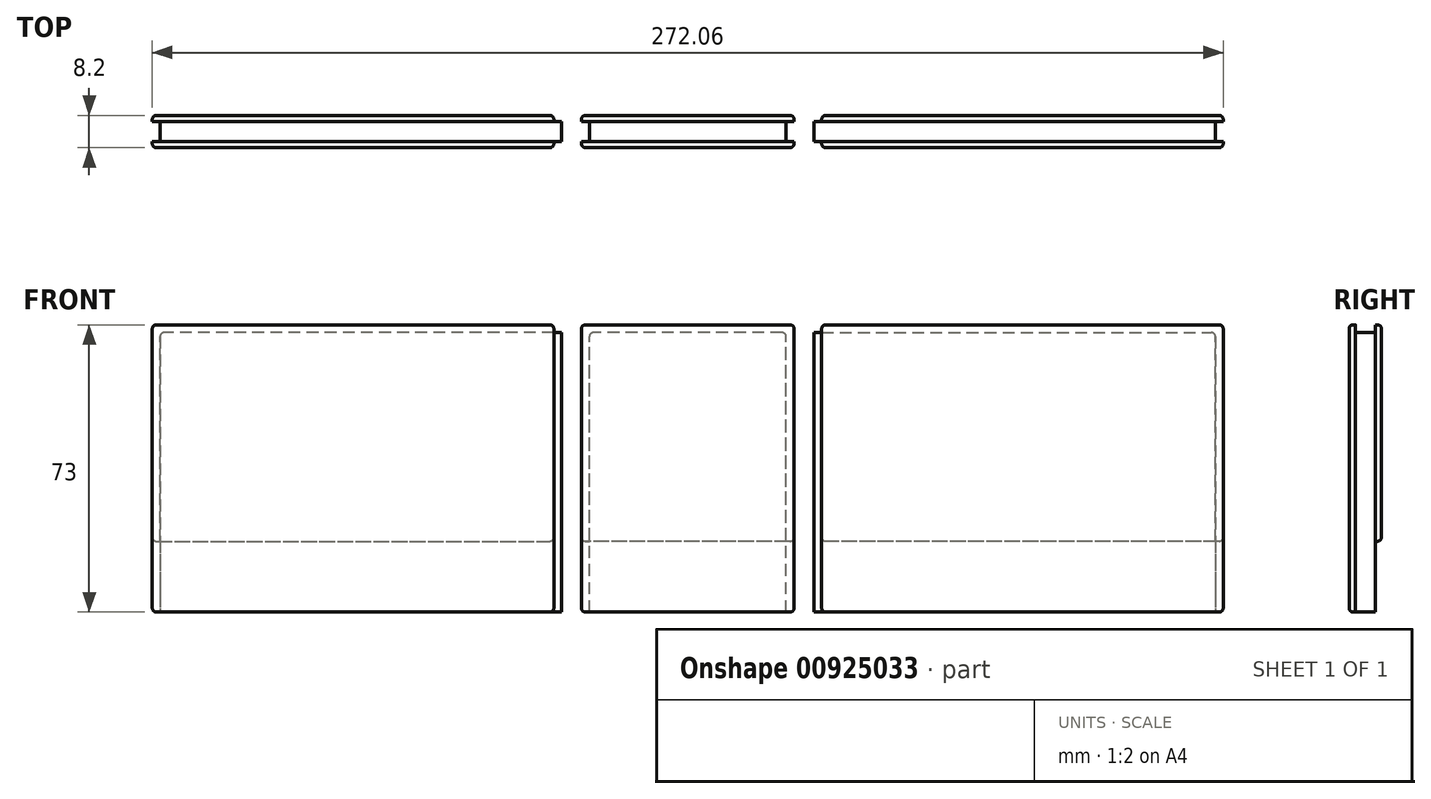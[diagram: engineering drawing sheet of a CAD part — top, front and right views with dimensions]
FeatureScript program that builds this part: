
annotation { "Feature Type Name" : "Feature", "Feature Type Description" : "" }
export const myFeature = defineFeature(function(context is Context, id is Id, definition is map)
    precondition{}
    {
        {
            var Q0;
            Q0=qCreatedBy(makeId("Front.planeOp"),FACE);
            var sketch = newSketch(context, id + "F0", { "sketchPlane" : qUnion([Q0])});
            skLineSegment(sketch, "E0.bottom", {"start": v(-25, 0) * mm, "end": v(25, 0) * mm});
            skLineSegment(sketch, "E0.top", {"start": v(-25, 18) * mm, "end": v(25, 18) * mm});
            skLineSegment(sketch, "E0.left", {"start": v(-25, 0) * mm, "end": v(-25, 18) * mm});
            skLineSegment(sketch, "E0.right", {"start": v(25, 0) * mm, "end": v(25, 18) * mm});
            skPoint(sketch, "E1", {"position": v(0, 18) * mm});
            skLineSegment(sketch, "E2.top", {"start": v(-25, 69) * mm, "end": v(25, 69) * mm});
            skLineSegment(sketch, "E2.left", {"start": v(-25, 18) * mm, "end": v(-25, 69) * mm});
            skLineSegment(sketch, "E2.right", {"start": v(25, 18) * mm, "end": v(25, 69) * mm});
            skSolve(sketch);
        }
        {
            var Q0;
            Q0=makeQuery(id+"F0.imprint","IMPRINT",FACE,{"disambiguationData":[TD([[makeQuery(id+"F0.imprint","IMPRINT",EDGE,{"derivedFrom":sQuery(id+"F0.wireOp",EDGE,"E0.top")}),1.0]])]});
            extrude(context, id + "F1", {"entities" : qUnion([Q0]), "depth" : 5 * mm, "offsetDistance" : 25 * mm});
        }
        {
            var Q0;
            Q0 = qSketchRegion(id + "F0", true);
            extrude(context, id + "F2", {"entities" : qUnion([Q0]), "operationType" : NewBodyOperationType.ADD, "depth" : 5 * mm, "offsetDistance" : 25 * mm});
        }
        {
            var Q0;
            {var subQ0=sQuery(id+"F0.wireOp",EDGE,"E2.right");var subQ1=sQuery(id+"F0.wireOp",EDGE,"E2.left");var subQ2=sQuery(id+"F0.wireOp",EDGE,"E2.top");Q0=makeQuery(id+"F2.boolean.opBoolean","MERGE",FACE,{"derivedFrom":[makeQuery(id+"F1.opExtrude","CAP_FACE",FACE,{"disambiguationData":[OSD([sQuery(id+"F0.wireOp",EDGE,"E0.top"),subQ2,subQ1,subQ0])],"isStart":true}),makeQuery(id+"F2.opExtrude","CAP_FACE",FACE,{"disambiguationData":[OSD([sQuery(id+"F0.wireOp",EDGE,"E0.bottom"),sQuery(id+"F0.wireOp",EDGE,"E0.left"),sQuery(id+"F0.wireOp",EDGE,"E0.right"),subQ2,subQ1,subQ0])],"isStart":true})]});}
            var sketch = newSketch(context, id + "F3", { "sketchPlane" : qUnion([Q0])});
            skLineSegment(sketch, "E3.bottom", {"start": v(-25, 69) * mm, "end": v(25, 69) * mm});
            skLineSegment(sketch, "E3.top", {"start": v(-25, 18) * mm, "end": v(25, 18) * mm});
            skLineSegment(sketch, "E3.left", {"start": v(-25, 69) * mm, "end": v(-25, 18) * mm});
            skLineSegment(sketch, "E3.right", {"start": v(25, 69) * mm, "end": v(25, 18) * mm});
            skSolve(sketch);
        }
        {
            var Q0;
            Q0=makeQuery(id+"F3.imprint","IMPRINT",FACE,{"disambiguationData":[TD([[makeQuery(id+"F3.imprint","IMPRINT",EDGE,{"derivedFrom":sQuery(id+"F3.wireOp",EDGE,"E3.bottom")}),1.0]])]});
            extrude(context, id + "F4", {"entities" : qUnion([Q0]), "operationType" : NewBodyOperationType.ADD, "depth" : 1.6 * mm, "offsetDistance" : 25 * mm});
        }
        {
            var Q0;
            {var subQ0=sQuery(id+"F0.wireOp",EDGE,"E2.right");var subQ1=sQuery(id+"F0.wireOp",EDGE,"E2.left");var subQ2=sQuery(id+"F0.wireOp",EDGE,"E2.top");Q0=makeQuery(id+"F2.boolean.opBoolean","MERGE",FACE,{"derivedFrom":[makeQuery(id+"F1.opExtrude","CAP_FACE",FACE,{"disambiguationData":[OSD([sQuery(id+"F0.wireOp",EDGE,"E0.top"),subQ2,subQ1,subQ0])],"isStart":false}),makeQuery(id+"F2.opExtrude","CAP_FACE",FACE,{"disambiguationData":[OSD([sQuery(id+"F0.wireOp",EDGE,"E0.bottom"),sQuery(id+"F0.wireOp",EDGE,"E0.left"),sQuery(id+"F0.wireOp",EDGE,"E0.right"),subQ2,subQ1,subQ0])],"isStart":false})]});}
            var sketch = newSketch(context, id + "F5", { "sketchPlane" : qUnion([Q0])});
            skLineSegment(sketch, "E4.bottom", {"start": v(-25, 69) * mm, "end": v(25, 69) * mm});
            skLineSegment(sketch, "E4.top", {"start": v(-25, 18) * mm, "end": v(25, 18) * mm});
            skLineSegment(sketch, "E4.left", {"start": v(-25, 69) * mm, "end": v(-25, 18) * mm});
            skLineSegment(sketch, "E4.right", {"start": v(25, 69) * mm, "end": v(25, 18) * mm});
            skSolve(sketch);
        }
        {
            var Q0;
            Q0=makeQuery(id+"F5.imprint","IMPRINT",FACE,{"disambiguationData":[TD([[makeQuery(id+"F5.imprint","IMPRINT",EDGE,{"derivedFrom":sQuery(id+"F5.wireOp",EDGE,"E4.bottom")}),-1.0]])]});
            extrude(context, id + "F6", {"entities" : qUnion([Q0]), "operationType" : NewBodyOperationType.ADD, "depth" : 1.6 * mm, "offsetDistance" : 25 * mm});
        }
        {
            var Q0;
            Q0=makeQuery(id+"F6.boolean.opBoolean","MERGE",FACE,{"derivedFrom":[makeQuery(id+"F4.boolean.opBoolean","MERGE",FACE,{"derivedFrom":[makeQuery(id+"F1.opExtrude","SWEPT_FACE",FACE,{"disambiguationData":[OSD([sQuery(id+"F0.wireOp",EDGE,"E2.top")])]}),makeQuery(id+"F4.opExtrude","SWEPT_FACE",FACE,{"disambiguationData":[OSD([sQuery(id+"F3.wireOp",EDGE,"E3.bottom")])]})]}),makeQuery(id+"F6.opExtrude","SWEPT_FACE",FACE,{"disambiguationData":[OSD([sQuery(id+"F5.wireOp",EDGE,"E4.bottom")])]})]});
            extrude(context, id + "F7", {"entities" : qUnion([Q0]), "operationType" : NewBodyOperationType.ADD, "depth" : 2 * mm, "offsetDistance" : 25 * mm});
        }
        {
            var Q0;
            {var subQ0=sQuery(id+"F5.wireOp",EDGE,"E4.left");var subQ1=sQuery(id+"F3.wireOp",EDGE,"E3.right");var subQ2=sQuery(id+"F0.wireOp",EDGE,"E2.left");Q0=makeQuery(id+"F7.boolean.opBoolean","MERGE",FACE,{"derivedFrom":[makeQuery(id+"F6.boolean.opBoolean","MERGE",FACE,{"derivedFrom":[makeQuery(id+"F4.boolean.opBoolean","MERGE",FACE,{"derivedFrom":[makeQuery(id+"F2.boolean.opBoolean","MERGE",FACE,{"derivedFrom":[makeQuery(id+"F1.opExtrude","SWEPT_FACE",FACE,{"disambiguationData":[OSD([subQ2])]}),makeQuery(id+"F2.opExtrude","SWEPT_FACE",FACE,{"disambiguationData":[OSD([sQuery(id+"F0.wireOp",EDGE,"E0.left"),subQ2])]})]}),makeQuery(id+"F4.opExtrude","SWEPT_FACE",FACE,{"disambiguationData":[OSD([subQ1])]})]}),makeQuery(id+"F6.opExtrude","SWEPT_FACE",FACE,{"disambiguationData":[OSD([subQ0])]})]}),makeQuery(id+"F7.opExtrude","SWEPT_FACE",FACE,{"disambiguationData":[OSD([sQuery(id+"F0.wireOp",EDGE,"E2.top"),subQ2,sQuery(id+"F3.wireOp",EDGE,"E3.bottom"),subQ1,sQuery(id+"F5.wireOp",EDGE,"E4.bottom"),subQ0])]})]});}
            var sketch = newSketch(context, id + "F8", { "sketchPlane" : qUnion([Q0])});
            skLineSegment(sketch, "E5", {"start": v(0, 18) * mm, "end": v(0, 71) * mm});
            skLineSegment(sketch, "E6", {"start": v(5, 18) * mm, "end": v(5, 71) * mm});
            skSolve(sketch);
        }
        {
            var Q0;
            Q0 = qSketchRegion(id + "F8", true);
            var Q1;
            {var subQ0=sQuery(id+"F8.wireOp",EDGE,"E5");Q1=makeQuery(id+"F8.imprint","IMPRINT",FACE,{"disambiguationData":[TD([[makeQuery(id+"F8.imprint","IMPRINT",EDGE,{"derivedFrom":subQ0}),1.0]])]});}
            var Q2;
            {var subQ0=sQuery(id+"F8.wireOp",EDGE,"E6");Q2=makeQuery(id+"F8.imprint","IMPRINT",FACE,{"disambiguationData":[TD([[makeQuery(id+"F8.imprint","IMPRINT",EDGE,{"derivedFrom":subQ0}),-1.0]])]});}
            extrude(context, id + "F9", {"entities" : qUnion([Q0, Q1, Q2]), "operationType" : NewBodyOperationType.ADD, "depth" : 2 * mm, "offsetDistance" : 25 * mm});
        }
        {
            var Q0;
            {var subQ0=sQuery(id+"F5.wireOp",EDGE,"E4.right");var subQ1=sQuery(id+"F3.wireOp",EDGE,"E3.left");var subQ2=sQuery(id+"F0.wireOp",EDGE,"E2.right");Q0=makeQuery(id+"F7.boolean.opBoolean","MERGE",FACE,{"derivedFrom":[makeQuery(id+"F6.boolean.opBoolean","MERGE",FACE,{"derivedFrom":[makeQuery(id+"F4.boolean.opBoolean","MERGE",FACE,{"derivedFrom":[makeQuery(id+"F2.boolean.opBoolean","MERGE",FACE,{"derivedFrom":[makeQuery(id+"F1.opExtrude","SWEPT_FACE",FACE,{"disambiguationData":[OSD([subQ2])]}),makeQuery(id+"F2.opExtrude","SWEPT_FACE",FACE,{"disambiguationData":[OSD([sQuery(id+"F0.wireOp",EDGE,"E0.right"),subQ2])]})]}),makeQuery(id+"F4.opExtrude","SWEPT_FACE",FACE,{"disambiguationData":[OSD([subQ1])]})]}),makeQuery(id+"F6.opExtrude","SWEPT_FACE",FACE,{"disambiguationData":[OSD([subQ0])]})]}),makeQuery(id+"F7.opExtrude","SWEPT_FACE",FACE,{"disambiguationData":[OSD([sQuery(id+"F0.wireOp",EDGE,"E2.top"),subQ2,sQuery(id+"F3.wireOp",EDGE,"E3.bottom"),subQ1,sQuery(id+"F5.wireOp",EDGE,"E4.bottom"),subQ0])]})]});}
            var sketch = newSketch(context, id + "F10", { "sketchPlane" : qUnion([Q0])});
            skLineSegment(sketch, "E7", {"start": v(-5, 18) * mm, "end": v(-5, 71) * mm});
            skLineSegment(sketch, "E8", {"start": v(0, 18) * mm, "end": v(0, 71) * mm});
            skSolve(sketch);
        }
        {
            var Q0;
            {var subQ0=sQuery(id+"F10.wireOp",EDGE,"E7");Q0=makeQuery(id+"F10.imprint","IMPRINT",FACE,{"disambiguationData":[TD([[makeQuery(id+"F10.imprint","IMPRINT",EDGE,{"derivedFrom":subQ0}),1.0]])]});}
            var Q1;
            {var subQ0=sQuery(id+"F10.wireOp",EDGE,"E8");Q1=makeQuery(id+"F10.imprint","IMPRINT",FACE,{"disambiguationData":[TD([[makeQuery(id+"F10.imprint","IMPRINT",EDGE,{"derivedFrom":subQ0}),-1.0]])]});}
            extrude(context, id + "F11", {"entities" : qUnion([Q0, Q1]), "operationType" : NewBodyOperationType.ADD, "depth" : 2 * mm, "offsetDistance" : 25 * mm});
        }
        {
            var Q0;
            {var subQ0=sQuery(id+"F0.wireOp",EDGE,"E2.right");var subQ1=sQuery(id+"F0.wireOp",EDGE,"E2.left");var subQ2=sQuery(id+"F0.wireOp",EDGE,"E2.top");Q0=makeQuery(id+"F2.boolean.opBoolean","MERGE",FACE,{"derivedFrom":[makeQuery(id+"F1.opExtrude","CAP_FACE",FACE,{"disambiguationData":[OSD([sQuery(id+"F0.wireOp",EDGE,"E0.top"),subQ2,subQ1,subQ0])],"isStart":false}),makeQuery(id+"F2.opExtrude","CAP_FACE",FACE,{"disambiguationData":[OSD([sQuery(id+"F0.wireOp",EDGE,"E0.bottom"),sQuery(id+"F0.wireOp",EDGE,"E0.left"),sQuery(id+"F0.wireOp",EDGE,"E0.right"),subQ2,subQ1,subQ0])],"isStart":false})]});}
            extrude(context, id + "F12", {"entities" : qUnion([Q0]), "operationType" : NewBodyOperationType.ADD, "depth" : 1.6 * mm, "offsetDistance" : 25 * mm});
        }
        {
            var Q0;
            {var subQ1=sQuery(id+"F5.wireOp",EDGE,"E4.right");var subQ5=sQuery(id+"F0.wireOp",EDGE,"E2.right");var subQ7=sQuery(id+"F0.wireOp",EDGE,"E2.left");var subQ8=sQuery(id+"F0.wireOp",EDGE,"E0.right");var subQ9=sQuery(id+"F0.wireOp",EDGE,"E0.left");var subQ10=sQuery(id+"F5.wireOp",EDGE,"E4.left");var subQ11=sQuery(id+"F5.wireOp",EDGE,"E4.top");Q0=makeQuery(id+"F12.boolean.opBoolean","SPLIT",FACE,{"disambiguationData":[TD([makeQuery(id+"F1.opExtrude","SWEPT_FACE",FACE,{"disambiguationData":[OSD([subQ5])]})])],"derivedFrom":makeQuery(id+"F11.boolean.opBoolean","MERGE",FACE,{"derivedFrom":[makeQuery(id+"F9.boolean.opBoolean","MERGE",FACE,{"derivedFrom":[makeQuery(id+"F6.opExtrude","SWEPT_FACE",FACE,{"disambiguationData":[OSD([subQ11])]}),makeQuery(id+"F9.opExtrude","SWEPT_FACE",FACE,{"disambiguationData":[OSD([subQ9,subQ7,subQ11,subQ10])]})]}),makeQuery(id+"F11.opExtrude","SWEPT_FACE",FACE,{"disambiguationData":[OSD([subQ8,subQ5,subQ11,subQ1])]})]})});}
            var Q1;
            {var subQ1=sQuery(id+"F5.wireOp",EDGE,"E4.left");var subQ2=sQuery(id+"F5.wireOp",EDGE,"E4.top");var subQ6=sQuery(id+"F0.wireOp",EDGE,"E2.left");var subQ8=sQuery(id+"F0.wireOp",EDGE,"E0.left");var subQ9=sQuery(id+"F5.wireOp",EDGE,"E4.right");var subQ10=sQuery(id+"F0.wireOp",EDGE,"E2.right");var subQ11=sQuery(id+"F0.wireOp",EDGE,"E0.right");Q1=makeQuery(id+"F12.boolean.opBoolean","SPLIT",FACE,{"disambiguationData":[TD([makeQuery(id+"F1.opExtrude","SWEPT_FACE",FACE,{"disambiguationData":[OSD([subQ6])]})])],"derivedFrom":makeQuery(id+"F11.boolean.opBoolean","MERGE",FACE,{"derivedFrom":[makeQuery(id+"F9.boolean.opBoolean","MERGE",FACE,{"derivedFrom":[makeQuery(id+"F6.opExtrude","SWEPT_FACE",FACE,{"disambiguationData":[OSD([subQ2])]}),makeQuery(id+"F9.opExtrude","SWEPT_FACE",FACE,{"disambiguationData":[OSD([subQ8,subQ6,subQ2,subQ1])]})]}),makeQuery(id+"F11.opExtrude","SWEPT_FACE",FACE,{"disambiguationData":[OSD([subQ11,subQ10,subQ2,subQ9])]})]})});}
            var Q2;
            {var subQ0=sQuery(id+"F0.wireOp",EDGE,"E0.bottom");Q2=makeQuery(id+"F12.boolean.opBoolean","MERGE",FACE,{"derivedFrom":[makeQuery(id+"F2.opExtrude","SWEPT_FACE",FACE,{"disambiguationData":[OSD([subQ0])]}),makeQuery(id+"F12.opExtrude","SWEPT_FACE",FACE,{"disambiguationData":[OSD([subQ0])]})]});}
            extrude(context, id + "F13", {"entities" : qUnion([Q0, Q1]), "operationType" : NewBodyOperationType.ADD, "endBound" : BoundingType.UP_TO_SURFACE, "depth" : 25 * mm, "endBoundEntityFace" : qUnion([Q2]), "offsetDistance" : 25 * mm});
        }
        {
            var Q0;
            {var subQ0=sQuery(id+"F5.wireOp",EDGE,"E4.right");var subQ1=sQuery(id+"F5.wireOp",EDGE,"E4.bottom");var subQ2=sQuery(id+"F3.wireOp",EDGE,"E3.left");var subQ3=sQuery(id+"F3.wireOp",EDGE,"E3.bottom");var subQ4=sQuery(id+"F0.wireOp",EDGE,"E2.right");var subQ5=sQuery(id+"F0.wireOp",EDGE,"E2.top");var subQ6=makeQuery(id+"F7.opExtrude","CAP_EDGE",EDGE,{"disambiguationData":[OSD([subQ5,subQ4,subQ3,subQ2,subQ1,subQ0])],"isStart":false});var subQ7=sQuery(id+"F5.wireOp",EDGE,"E4.left");var subQ8=sQuery(id+"F3.wireOp",EDGE,"E3.right");var subQ9=sQuery(id+"F0.wireOp",EDGE,"E2.left");var subQ10=makeQuery(id+"F7.opExtrude","CAP_EDGE",EDGE,{"disambiguationData":[OSD([subQ5,subQ9,subQ3,subQ8,subQ1,subQ7])],"isStart":false});Q0=makeQuery(id+"F11.boolean.opBoolean","MERGE",FACE,{"derivedFrom":[makeQuery(id+"F9.boolean.opBoolean","MERGE",FACE,{"derivedFrom":[makeQuery(id+"F7.opExtrude","CAP_FACE",FACE,{"disambiguationData":[OSD([subQ5,subQ3,subQ1])],"isStart":false}),makeQuery(id+"F9.opExtrude","SWEPT_FACE",FACE,{"disambiguationData":[OSD([subQ5,subQ9,subQ3,subQ8,subQ1,subQ7]),TDD([makeQuery(id+"F8.imprint","IMPRINT",EDGE,{"disambiguationData":[TD([[makeQuery(id+"F8.imprint","INTERSECT",VERTEX,{"derivedFrom":[subQ10,sQuery(id+"F8.wireOp",EDGE,"E5")]}),-1.0]])],"derivedFrom":subQ10})])]}),makeQuery(id+"F9.opExtrude","SWEPT_FACE",FACE,{"disambiguationData":[OSD([subQ5,subQ9,subQ3,subQ8,subQ1,subQ7]),TDD([makeQuery(id+"F8.imprint","IMPRINT",EDGE,{"disambiguationData":[TD([[makeQuery(id+"F8.imprint","INTERSECT",VERTEX,{"derivedFrom":[subQ10,sQuery(id+"F8.wireOp",EDGE,"E6")]}),1.0]])],"derivedFrom":subQ10})])]})]}),makeQuery(id+"F11.opExtrude","SWEPT_FACE",FACE,{"disambiguationData":[OSD([subQ5,subQ4,subQ3,subQ2,subQ1,subQ0]),TDD([makeQuery(id+"F10.imprint","IMPRINT",EDGE,{"disambiguationData":[TD([[makeQuery(id+"F10.imprint","INTERSECT",VERTEX,{"derivedFrom":[subQ6,sQuery(id+"F10.wireOp",EDGE,"E8")]}),-1.0]])],"derivedFrom":subQ6})])]}),makeQuery(id+"F11.opExtrude","SWEPT_FACE",FACE,{"disambiguationData":[OSD([subQ5,subQ4,subQ3,subQ2,subQ1,subQ0]),TDD([makeQuery(id+"F10.imprint","IMPRINT",EDGE,{"disambiguationData":[TD([[makeQuery(id+"F10.imprint","INTERSECT",VERTEX,{"derivedFrom":[subQ6,sQuery(id+"F10.wireOp",EDGE,"E7")]}),1.0]])],"derivedFrom":subQ6})])]})]});}
            var sketch = newSketch(context, id + "F14", { "sketchPlane" : qUnion([Q0])});
            skLineSegment(sketch, "E9", {"start": v(-25, 0) * mm, "end": v(25, 0) * mm});
            skLineSegment(sketch, "E10", {"start": v(25, -5) * mm, "end": v(-25, -5) * mm});
            skSolve(sketch);
        }
        {
            var Q0;
            Q0=makeQuery(id+"F14.imprint","IMPRINT",FACE,{"disambiguationData":[TD([[makeQuery(id+"F14.imprint","IMPRINT",EDGE,{"derivedFrom":sQuery(id+"F14.wireOp",EDGE,"E10")}),1.0]])]});
            var Q1;
            Q1=makeQuery(id+"F14.imprint","IMPRINT",FACE,{"disambiguationData":[TD([[makeQuery(id+"F14.imprint","IMPRINT",EDGE,{"derivedFrom":sQuery(id+"F14.wireOp",EDGE,"E9")}),1.0]])]});
            extrude(context, id + "F15", {"entities" : qUnion([Q0, Q1]), "operationType" : NewBodyOperationType.ADD, "depth" : 2 * mm, "offsetDistance" : 25 * mm});
        }
        {
            var Q0;
            Q0=makeQuery(id+"F11.opExtrude","CAP_EDGE",EDGE,{"disambiguationData":[OSD([sQuery(id+"F3.wireOp",EDGE,"E3.bottom"),sQuery(id+"F3.wireOp",EDGE,"E3.left")])],"isStart":false});
            var Q1;
            Q1=makeQuery(id+"F11.opExtrude","CAP_EDGE",EDGE,{"disambiguationData":[OSD([sQuery(id+"F5.wireOp",EDGE,"E4.bottom"),sQuery(id+"F5.wireOp",EDGE,"E4.right")])],"isStart":false});
            var Q2;
            Q2=makeQuery(id+"F9.opExtrude","CAP_EDGE",EDGE,{"disambiguationData":[OSD([sQuery(id+"F5.wireOp",EDGE,"E4.bottom"),sQuery(id+"F5.wireOp",EDGE,"E4.left")])],"isStart":false});
            var Q3;
            Q3=makeQuery(id+"F9.opExtrude","CAP_EDGE",EDGE,{"disambiguationData":[OSD([sQuery(id+"F3.wireOp",EDGE,"E3.bottom"),sQuery(id+"F3.wireOp",EDGE,"E3.right")])],"isStart":false});
            var Q4;
            {var subQ0=sQuery(id+"F3.wireOp",EDGE,"E3.top");var subQ1=sQuery(id+"F3.wireOp",EDGE,"E3.bottom");Q4=makeQuery(id+"F11.boolean.opBoolean","MERGE",EDGE,{"derivedFrom":[makeQuery(id+"F9.boolean.opBoolean","MERGE",EDGE,{"derivedFrom":[makeQuery(id+"F4.opExtrude","CAP_EDGE",EDGE,{"disambiguationData":[OSD([subQ0])],"isStart":false}),makeQuery(id+"F9.opExtrude","SWEPT_EDGE",EDGE,{"disambiguationData":[OSD([sQuery(id+"F0.wireOp",EDGE,"E0.left"),sQuery(id+"F0.wireOp",EDGE,"E2.left"),subQ1,subQ0,sQuery(id+"F3.wireOp",EDGE,"E3.right")])]})]}),makeQuery(id+"F11.opExtrude","SWEPT_EDGE",EDGE,{"disambiguationData":[OSD([sQuery(id+"F0.wireOp",EDGE,"E0.right"),sQuery(id+"F0.wireOp",EDGE,"E2.right"),subQ1,subQ0,sQuery(id+"F3.wireOp",EDGE,"E3.left")])]})]});}
            var Q5;
            {var subQ0=sQuery(id+"F5.wireOp",EDGE,"E4.top");var subQ1=sQuery(id+"F5.wireOp",EDGE,"E4.bottom");Q5=makeQuery(id+"F11.boolean.opBoolean","MERGE",EDGE,{"derivedFrom":[makeQuery(id+"F9.boolean.opBoolean","MERGE",EDGE,{"derivedFrom":[makeQuery(id+"F6.opExtrude","CAP_EDGE",EDGE,{"disambiguationData":[OSD([subQ0])],"isStart":false}),makeQuery(id+"F9.opExtrude","SWEPT_EDGE",EDGE,{"disambiguationData":[OSD([sQuery(id+"F0.wireOp",EDGE,"E0.left"),sQuery(id+"F0.wireOp",EDGE,"E2.left"),subQ1,subQ0,sQuery(id+"F5.wireOp",EDGE,"E4.left")])]})]}),makeQuery(id+"F11.opExtrude","SWEPT_EDGE",EDGE,{"disambiguationData":[OSD([sQuery(id+"F0.wireOp",EDGE,"E0.right"),sQuery(id+"F0.wireOp",EDGE,"E2.right"),subQ1,subQ0,sQuery(id+"F5.wireOp",EDGE,"E4.right")])]})]});}
            var Q6;
            Q6=makeQuery(id+"F7.opExtrude","CAP_EDGE",EDGE,{"disambiguationData":[OSD([sQuery(id+"F0.wireOp",EDGE,"E2.top"),sQuery(id+"F0.wireOp",EDGE,"E2.left"),sQuery(id+"F3.wireOp",EDGE,"E3.bottom"),sQuery(id+"F3.wireOp",EDGE,"E3.right"),sQuery(id+"F5.wireOp",EDGE,"E4.bottom"),sQuery(id+"F5.wireOp",EDGE,"E4.left")])],"isStart":false});
            var Q7;
            Q7=makeQuery(id+"F7.opExtrude","CAP_EDGE",EDGE,{"disambiguationData":[OSD([sQuery(id+"F0.wireOp",EDGE,"E2.top"),sQuery(id+"F0.wireOp",EDGE,"E2.right"),sQuery(id+"F3.wireOp",EDGE,"E3.bottom"),sQuery(id+"F3.wireOp",EDGE,"E3.left"),sQuery(id+"F5.wireOp",EDGE,"E4.bottom"),sQuery(id+"F5.wireOp",EDGE,"E4.right")])],"isStart":false});
            var Q8;
            {var subQ0=sQuery(id+"F3.wireOp",EDGE,"E3.left");var subQ1=sQuery(id+"F3.wireOp",EDGE,"E3.bottom");var subQ2=sQuery(id+"F5.wireOp",EDGE,"E4.right");var subQ3=sQuery(id+"F5.wireOp",EDGE,"E4.bottom");var subQ4=sQuery(id+"F0.wireOp",EDGE,"E2.right");var subQ5=sQuery(id+"F0.wireOp",EDGE,"E2.top");var subQ6=sQuery(id+"F3.wireOp",EDGE,"E3.right");var subQ7=sQuery(id+"F5.wireOp",EDGE,"E4.left");var subQ8=sQuery(id+"F0.wireOp",EDGE,"E2.left");Q8=makeQuery(id+"F11.boolean.opBoolean","MERGE",EDGE,{"derivedFrom":[makeQuery(id+"F9.boolean.opBoolean","MERGE",EDGE,{"derivedFrom":[makeQuery(id+"F7.opExtrude","CAP_EDGE",EDGE,{"disambiguationData":[OSD([subQ1])],"isStart":false}),makeQuery(id+"F9.opExtrude","SWEPT_EDGE",EDGE,{"disambiguationData":[OSD([subQ5,subQ8,subQ1,subQ6,subQ3,subQ7]),TDD([makeQuery(id+"F8.imprint","INTERSECT",VERTEX,{"derivedFrom":[makeQuery(id+"F7.opExtrude","CAP_EDGE",EDGE,{"disambiguationData":[OSD([subQ5,subQ8,subQ1,subQ6,subQ3,subQ7])],"isStart":false}),makeQuery(id+"F7.boolean.opBoolean","MERGE",EDGE,{"derivedFrom":[makeQuery(id+"F4.opExtrude","CAP_EDGE",EDGE,{"disambiguationData":[OSD([subQ6])],"isStart":false}),makeQuery(id+"F7.opExtrude","SWEPT_EDGE",EDGE,{"disambiguationData":[OSD([subQ1,subQ6])]})]})]})])]})]}),makeQuery(id+"F11.opExtrude","SWEPT_EDGE",EDGE,{"disambiguationData":[OSD([subQ5,subQ4,subQ1,subQ0,subQ3,subQ2]),TDD([makeQuery(id+"F10.imprint","INTERSECT",VERTEX,{"derivedFrom":[makeQuery(id+"F7.opExtrude","CAP_EDGE",EDGE,{"disambiguationData":[OSD([subQ5,subQ4,subQ1,subQ0,subQ3,subQ2])],"isStart":false}),makeQuery(id+"F7.boolean.opBoolean","MERGE",EDGE,{"derivedFrom":[makeQuery(id+"F4.opExtrude","CAP_EDGE",EDGE,{"disambiguationData":[OSD([subQ0])],"isStart":false}),makeQuery(id+"F7.opExtrude","SWEPT_EDGE",EDGE,{"disambiguationData":[OSD([subQ1,subQ0])]})]})]})])]})]});}
            var Q9;
            {var subQ0=sQuery(id+"F5.wireOp",EDGE,"E4.right");var subQ1=sQuery(id+"F5.wireOp",EDGE,"E4.bottom");var subQ2=sQuery(id+"F3.wireOp",EDGE,"E3.left");var subQ3=sQuery(id+"F3.wireOp",EDGE,"E3.bottom");var subQ4=sQuery(id+"F0.wireOp",EDGE,"E2.right");var subQ5=sQuery(id+"F0.wireOp",EDGE,"E2.top");var subQ6=sQuery(id+"F5.wireOp",EDGE,"E4.left");var subQ7=sQuery(id+"F3.wireOp",EDGE,"E3.right");var subQ8=sQuery(id+"F0.wireOp",EDGE,"E2.left");Q9=makeQuery(id+"F11.boolean.opBoolean","MERGE",EDGE,{"derivedFrom":[makeQuery(id+"F9.boolean.opBoolean","MERGE",EDGE,{"derivedFrom":[makeQuery(id+"F7.opExtrude","CAP_EDGE",EDGE,{"disambiguationData":[OSD([subQ1])],"isStart":false}),makeQuery(id+"F9.opExtrude","SWEPT_EDGE",EDGE,{"disambiguationData":[OSD([subQ5,subQ8,subQ3,subQ7,subQ1,subQ6]),TDD([makeQuery(id+"F8.imprint","INTERSECT",VERTEX,{"derivedFrom":[makeQuery(id+"F7.opExtrude","CAP_EDGE",EDGE,{"disambiguationData":[OSD([subQ5,subQ8,subQ3,subQ7,subQ1,subQ6])],"isStart":false}),makeQuery(id+"F7.boolean.opBoolean","MERGE",EDGE,{"derivedFrom":[makeQuery(id+"F6.opExtrude","CAP_EDGE",EDGE,{"disambiguationData":[OSD([subQ6])],"isStart":false}),makeQuery(id+"F7.opExtrude","SWEPT_EDGE",EDGE,{"disambiguationData":[OSD([subQ1,subQ6])]})]})]})])]})]}),makeQuery(id+"F11.opExtrude","SWEPT_EDGE",EDGE,{"disambiguationData":[OSD([subQ5,subQ4,subQ3,subQ2,subQ1,subQ0]),TDD([makeQuery(id+"F10.imprint","INTERSECT",VERTEX,{"derivedFrom":[makeQuery(id+"F7.opExtrude","CAP_EDGE",EDGE,{"disambiguationData":[OSD([subQ5,subQ4,subQ3,subQ2,subQ1,subQ0])],"isStart":false}),makeQuery(id+"F7.boolean.opBoolean","MERGE",EDGE,{"derivedFrom":[makeQuery(id+"F6.opExtrude","CAP_EDGE",EDGE,{"disambiguationData":[OSD([subQ0])],"isStart":false}),makeQuery(id+"F7.opExtrude","SWEPT_EDGE",EDGE,{"disambiguationData":[OSD([subQ1,subQ0])]})]})]})])]})]});}
            var Q10;
            {var subQ0=sQuery(id+"F3.wireOp",EDGE,"E3.right");var subQ1=sQuery(id+"F3.wireOp",EDGE,"E3.bottom");var subQ2=sQuery(id+"F5.wireOp",EDGE,"E4.left");var subQ3=sQuery(id+"F5.wireOp",EDGE,"E4.bottom");var subQ4=sQuery(id+"F0.wireOp",EDGE,"E2.left");var subQ5=sQuery(id+"F0.wireOp",EDGE,"E2.top");var subQ6=makeQuery(id+"F7.opExtrude","CAP_EDGE",EDGE,{"disambiguationData":[OSD([subQ5,subQ4,subQ1,subQ0,subQ3,subQ2])],"isStart":false});Q10=makeQuery(id+"F9.opExtrude","CAP_EDGE",EDGE,{"disambiguationData":[OSD([subQ5,subQ4,subQ1,subQ0,subQ3,subQ2]),TDD([makeQuery(id+"F8.imprint","IMPRINT",EDGE,{"disambiguationData":[TD([[makeQuery(id+"F8.imprint","INTERSECT",VERTEX,{"derivedFrom":[subQ6,sQuery(id+"F8.wireOp",EDGE,"E5")]}),-1.0]])],"derivedFrom":subQ6})])],"isStart":false});}
            var Q11;
            {var subQ0=sQuery(id+"F5.wireOp",EDGE,"E4.left");var subQ1=sQuery(id+"F5.wireOp",EDGE,"E4.bottom");var subQ2=sQuery(id+"F3.wireOp",EDGE,"E3.right");var subQ3=sQuery(id+"F3.wireOp",EDGE,"E3.bottom");var subQ4=sQuery(id+"F0.wireOp",EDGE,"E2.left");var subQ5=sQuery(id+"F0.wireOp",EDGE,"E2.top");var subQ6=makeQuery(id+"F7.opExtrude","CAP_EDGE",EDGE,{"disambiguationData":[OSD([subQ5,subQ4,subQ3,subQ2,subQ1,subQ0])],"isStart":false});Q11=makeQuery(id+"F9.opExtrude","CAP_EDGE",EDGE,{"disambiguationData":[OSD([subQ5,subQ4,subQ3,subQ2,subQ1,subQ0]),TDD([makeQuery(id+"F8.imprint","IMPRINT",EDGE,{"disambiguationData":[TD([[makeQuery(id+"F8.imprint","INTERSECT",VERTEX,{"derivedFrom":[subQ6,sQuery(id+"F8.wireOp",EDGE,"E6")]}),1.0]])],"derivedFrom":subQ6})])],"isStart":false});}
            var Q12;
            {var subQ0=sQuery(id+"F3.wireOp",EDGE,"E3.left");var subQ1=sQuery(id+"F3.wireOp",EDGE,"E3.bottom");var subQ2=sQuery(id+"F5.wireOp",EDGE,"E4.right");var subQ3=sQuery(id+"F5.wireOp",EDGE,"E4.bottom");var subQ4=sQuery(id+"F0.wireOp",EDGE,"E2.right");var subQ5=sQuery(id+"F0.wireOp",EDGE,"E2.top");var subQ6=makeQuery(id+"F7.opExtrude","CAP_EDGE",EDGE,{"disambiguationData":[OSD([subQ5,subQ4,subQ1,subQ0,subQ3,subQ2])],"isStart":false});Q12=makeQuery(id+"F11.opExtrude","CAP_EDGE",EDGE,{"disambiguationData":[OSD([subQ5,subQ4,subQ1,subQ0,subQ3,subQ2]),TDD([makeQuery(id+"F10.imprint","IMPRINT",EDGE,{"disambiguationData":[TD([[makeQuery(id+"F10.imprint","INTERSECT",VERTEX,{"derivedFrom":[subQ6,sQuery(id+"F10.wireOp",EDGE,"E8")]}),-1.0]])],"derivedFrom":subQ6})])],"isStart":false});}
            var Q13;
            {var subQ0=sQuery(id+"F5.wireOp",EDGE,"E4.right");var subQ1=sQuery(id+"F5.wireOp",EDGE,"E4.bottom");var subQ2=sQuery(id+"F3.wireOp",EDGE,"E3.left");var subQ3=sQuery(id+"F3.wireOp",EDGE,"E3.bottom");var subQ4=sQuery(id+"F0.wireOp",EDGE,"E2.right");var subQ5=sQuery(id+"F0.wireOp",EDGE,"E2.top");var subQ6=makeQuery(id+"F7.opExtrude","CAP_EDGE",EDGE,{"disambiguationData":[OSD([subQ5,subQ4,subQ3,subQ2,subQ1,subQ0])],"isStart":false});Q13=makeQuery(id+"F11.opExtrude","CAP_EDGE",EDGE,{"disambiguationData":[OSD([subQ5,subQ4,subQ3,subQ2,subQ1,subQ0]),TDD([makeQuery(id+"F10.imprint","IMPRINT",EDGE,{"disambiguationData":[TD([[makeQuery(id+"F10.imprint","INTERSECT",VERTEX,{"derivedFrom":[subQ6,sQuery(id+"F10.wireOp",EDGE,"E7")]}),1.0]])],"derivedFrom":subQ6})])],"isStart":false});}
            var Q14;
            {var subQ0=sQuery(id+"F5.wireOp",EDGE,"E4.left");var subQ1=sQuery(id+"F5.wireOp",EDGE,"E4.bottom");var subQ3=sQuery(id+"F5.wireOp",EDGE,"E4.right");var subQ6=sQuery(id+"F0.wireOp",EDGE,"E2.right");var subQ8=sQuery(id+"F0.wireOp",EDGE,"E2.left");var subQ9=sQuery(id+"F0.wireOp",EDGE,"E0.right");var subQ10=sQuery(id+"F0.wireOp",EDGE,"E0.left");var subQ11=sQuery(id+"F0.wireOp",EDGE,"E0.bottom");var subQ13=sQuery(id+"F5.wireOp",EDGE,"E4.top");var subQ20=makeQuery(id+"F11.boolean.opBoolean","MERGE",EDGE,{"derivedFrom":[makeQuery(id+"F9.boolean.opBoolean","MERGE",EDGE,{"derivedFrom":[makeQuery(id+"F6.opExtrude","CAP_EDGE",EDGE,{"disambiguationData":[OSD([subQ13])],"isStart":false}),makeQuery(id+"F9.opExtrude","SWEPT_EDGE",EDGE,{"disambiguationData":[OSD([subQ10,subQ8,subQ1,subQ13,subQ0])]})]}),makeQuery(id+"F11.opExtrude","SWEPT_EDGE",EDGE,{"disambiguationData":[OSD([subQ9,subQ6,subQ1,subQ13,subQ3])]})]});Q14=makeQuery(id+"F13.boolean.opBoolean","MERGE",EDGE,{"derivedFrom":[makeQuery(id+"F12.opExtrude","CAP_EDGE",EDGE,{"disambiguationData":[OSD([subQ11])],"isStart":false}),makeQuery(id+"F13.opExtrude","CAP_EDGE",EDGE,{"disambiguationData":[OSD([subQ10,subQ9,subQ8,subQ6,subQ1,subQ13,subQ0,subQ3]),TDD([makeQuery(id+"F12.boolean.opBoolean","SPLIT",EDGE,{"disambiguationData":[TD([makeQuery(id+"F1.opExtrude","SWEPT_FACE",FACE,{"disambiguationData":[OSD([subQ8])]})])],"derivedFrom":subQ20})])],"isStart":false}),makeQuery(id+"F13.opExtrude","CAP_EDGE",EDGE,{"disambiguationData":[OSD([subQ10,subQ9,subQ8,subQ6,subQ1,subQ13,subQ0,subQ3]),TDD([makeQuery(id+"F12.boolean.opBoolean","SPLIT",EDGE,{"disambiguationData":[TD([makeQuery(id+"F1.opExtrude","SWEPT_FACE",FACE,{"disambiguationData":[OSD([subQ6])]})])],"derivedFrom":subQ20})])],"isStart":false})]});}
            var Q15;
            Q15=makeQuery(id+"F13.opExtrude","CAP_EDGE",EDGE,{"disambiguationData":[OSD([sQuery(id+"F0.wireOp",EDGE,"E0.left"),sQuery(id+"F0.wireOp",EDGE,"E2.left"),sQuery(id+"F5.wireOp",EDGE,"E4.top"),sQuery(id+"F5.wireOp",EDGE,"E4.left")])],"isStart":false});
            var Q16;
            Q16=makeQuery(id+"F13.opExtrude","CAP_EDGE",EDGE,{"disambiguationData":[OSD([sQuery(id+"F0.wireOp",EDGE,"E0.right"),sQuery(id+"F0.wireOp",EDGE,"E2.right"),sQuery(id+"F5.wireOp",EDGE,"E4.top"),sQuery(id+"F5.wireOp",EDGE,"E4.right")])],"isStart":false});
            var Q17;
            Q17=makeQuery(id+"F9.opExtrude","CAP_EDGE",EDGE,{"disambiguationData":[OSD([sQuery(id+"F0.wireOp",EDGE,"E0.left"),sQuery(id+"F0.wireOp",EDGE,"E2.left"),sQuery(id+"F3.wireOp",EDGE,"E3.top"),sQuery(id+"F3.wireOp",EDGE,"E3.right")])],"isStart":false});
            var Q18;
            Q18=makeQuery(id+"F11.opExtrude","CAP_EDGE",EDGE,{"disambiguationData":[OSD([sQuery(id+"F0.wireOp",EDGE,"E0.right"),sQuery(id+"F0.wireOp",EDGE,"E2.right"),sQuery(id+"F3.wireOp",EDGE,"E3.top"),sQuery(id+"F3.wireOp",EDGE,"E3.left")])],"isStart":false});
            var Q19;
            {var subQ0=sQuery(id+"F5.wireOp",EDGE,"E4.right");var subQ1=sQuery(id+"F5.wireOp",EDGE,"E4.bottom");var subQ2=sQuery(id+"F3.wireOp",EDGE,"E3.left");var subQ3=sQuery(id+"F3.wireOp",EDGE,"E3.bottom");var subQ4=sQuery(id+"F0.wireOp",EDGE,"E2.right");var subQ5=sQuery(id+"F0.wireOp",EDGE,"E2.top");var subQ6=sQuery(id+"F5.wireOp",EDGE,"E4.left");var subQ7=sQuery(id+"F3.wireOp",EDGE,"E3.right");var subQ8=sQuery(id+"F0.wireOp",EDGE,"E2.left");Q19=makeQuery(id+"F15.opExtrude","CAP_EDGE",EDGE,{"disambiguationData":[OSD([subQ5,subQ8,subQ4,subQ3,subQ2,subQ7,subQ1,subQ6,subQ0]),TDD([makeQuery(id+"F14.imprint","IMPRINT",EDGE,{"derivedFrom":makeQuery(id+"F11.boolean.opBoolean","MERGE",EDGE,{"derivedFrom":[makeQuery(id+"F9.boolean.opBoolean","MERGE",EDGE,{"derivedFrom":[makeQuery(id+"F7.opExtrude","CAP_EDGE",EDGE,{"disambiguationData":[OSD([subQ1])],"isStart":false}),makeQuery(id+"F9.opExtrude","SWEPT_EDGE",EDGE,{"disambiguationData":[OSD([subQ5,subQ8,subQ3,subQ7,subQ1,subQ6]),TDD([makeQuery(id+"F8.imprint","INTERSECT",VERTEX,{"derivedFrom":[makeQuery(id+"F7.opExtrude","CAP_EDGE",EDGE,{"disambiguationData":[OSD([subQ5,subQ8,subQ3,subQ7,subQ1,subQ6])],"isStart":false}),makeQuery(id+"F7.boolean.opBoolean","MERGE",EDGE,{"derivedFrom":[makeQuery(id+"F6.opExtrude","CAP_EDGE",EDGE,{"disambiguationData":[OSD([subQ6])],"isStart":false}),makeQuery(id+"F7.opExtrude","SWEPT_EDGE",EDGE,{"disambiguationData":[OSD([subQ1,subQ6])]})]})]})])]})]}),makeQuery(id+"F11.opExtrude","SWEPT_EDGE",EDGE,{"disambiguationData":[OSD([subQ5,subQ4,subQ3,subQ2,subQ1,subQ0]),TDD([makeQuery(id+"F10.imprint","INTERSECT",VERTEX,{"derivedFrom":[makeQuery(id+"F7.opExtrude","CAP_EDGE",EDGE,{"disambiguationData":[OSD([subQ5,subQ4,subQ3,subQ2,subQ1,subQ0])],"isStart":false}),makeQuery(id+"F7.boolean.opBoolean","MERGE",EDGE,{"derivedFrom":[makeQuery(id+"F6.opExtrude","CAP_EDGE",EDGE,{"disambiguationData":[OSD([subQ0])],"isStart":false}),makeQuery(id+"F7.opExtrude","SWEPT_EDGE",EDGE,{"disambiguationData":[OSD([subQ1,subQ0])]})]})]})])]})]})})])],"isStart":false});}
            var Q20;
            {var subQ0=sQuery(id+"F3.wireOp",EDGE,"E3.left");var subQ1=sQuery(id+"F3.wireOp",EDGE,"E3.bottom");var subQ2=sQuery(id+"F5.wireOp",EDGE,"E4.right");var subQ3=sQuery(id+"F5.wireOp",EDGE,"E4.bottom");var subQ4=sQuery(id+"F0.wireOp",EDGE,"E2.right");var subQ5=sQuery(id+"F0.wireOp",EDGE,"E2.top");var subQ6=sQuery(id+"F3.wireOp",EDGE,"E3.right");var subQ7=sQuery(id+"F5.wireOp",EDGE,"E4.left");var subQ8=sQuery(id+"F0.wireOp",EDGE,"E2.left");Q20=makeQuery(id+"F15.opExtrude","CAP_EDGE",EDGE,{"disambiguationData":[OSD([subQ5,subQ8,subQ4,subQ1,subQ0,subQ6,subQ3,subQ7,subQ2]),TDD([makeQuery(id+"F14.imprint","IMPRINT",EDGE,{"derivedFrom":makeQuery(id+"F11.boolean.opBoolean","MERGE",EDGE,{"derivedFrom":[makeQuery(id+"F9.boolean.opBoolean","MERGE",EDGE,{"derivedFrom":[makeQuery(id+"F7.opExtrude","CAP_EDGE",EDGE,{"disambiguationData":[OSD([subQ1])],"isStart":false}),makeQuery(id+"F9.opExtrude","SWEPT_EDGE",EDGE,{"disambiguationData":[OSD([subQ5,subQ8,subQ1,subQ6,subQ3,subQ7]),TDD([makeQuery(id+"F8.imprint","INTERSECT",VERTEX,{"derivedFrom":[makeQuery(id+"F7.opExtrude","CAP_EDGE",EDGE,{"disambiguationData":[OSD([subQ5,subQ8,subQ1,subQ6,subQ3,subQ7])],"isStart":false}),makeQuery(id+"F7.boolean.opBoolean","MERGE",EDGE,{"derivedFrom":[makeQuery(id+"F4.opExtrude","CAP_EDGE",EDGE,{"disambiguationData":[OSD([subQ6])],"isStart":false}),makeQuery(id+"F7.opExtrude","SWEPT_EDGE",EDGE,{"disambiguationData":[OSD([subQ1,subQ6])]})]})]})])]})]}),makeQuery(id+"F11.opExtrude","SWEPT_EDGE",EDGE,{"disambiguationData":[OSD([subQ5,subQ4,subQ1,subQ0,subQ3,subQ2]),TDD([makeQuery(id+"F10.imprint","INTERSECT",VERTEX,{"derivedFrom":[makeQuery(id+"F7.opExtrude","CAP_EDGE",EDGE,{"disambiguationData":[OSD([subQ5,subQ4,subQ1,subQ0,subQ3,subQ2])],"isStart":false}),makeQuery(id+"F7.boolean.opBoolean","MERGE",EDGE,{"derivedFrom":[makeQuery(id+"F4.opExtrude","CAP_EDGE",EDGE,{"disambiguationData":[OSD([subQ0])],"isStart":false}),makeQuery(id+"F7.opExtrude","SWEPT_EDGE",EDGE,{"disambiguationData":[OSD([subQ1,subQ0])]})]})]})])]})]})})])],"isStart":false});}
            var Q21;
            {var subQ0=sQuery(id+"F5.wireOp",EDGE,"E4.right");var subQ1=sQuery(id+"F5.wireOp",EDGE,"E4.bottom");var subQ2=sQuery(id+"F3.wireOp",EDGE,"E3.left");var subQ3=sQuery(id+"F3.wireOp",EDGE,"E3.bottom");var subQ4=sQuery(id+"F0.wireOp",EDGE,"E2.right");var subQ5=sQuery(id+"F0.wireOp",EDGE,"E2.top");var subQ6=makeQuery(id+"F7.opExtrude","CAP_EDGE",EDGE,{"disambiguationData":[OSD([subQ5,subQ4,subQ3,subQ2,subQ1,subQ0])],"isStart":false});Q21=makeQuery(id+"F15.opExtrude","CAP_EDGE",EDGE,{"disambiguationData":[OSD([subQ5,subQ4,subQ3,subQ2,subQ1,subQ0]),TDD([makeQuery(id+"F14.imprint","IMPRINT",EDGE,{"derivedFrom":makeQuery(id+"F11.opExtrude","CAP_EDGE",EDGE,{"disambiguationData":[OSD([subQ5,subQ4,subQ3,subQ2,subQ1,subQ0]),TDD([makeQuery(id+"F10.imprint","IMPRINT",EDGE,{"disambiguationData":[TD([[makeQuery(id+"F10.imprint","INTERSECT",VERTEX,{"derivedFrom":[subQ6,sQuery(id+"F10.wireOp",EDGE,"E7")]}),1.0]])],"derivedFrom":subQ6})])],"isStart":false})})])],"isStart":false});}
            var Q22;
            {var subQ0=sQuery(id+"F3.wireOp",EDGE,"E3.left");var subQ1=sQuery(id+"F3.wireOp",EDGE,"E3.bottom");var subQ2=sQuery(id+"F5.wireOp",EDGE,"E4.right");var subQ3=sQuery(id+"F5.wireOp",EDGE,"E4.bottom");var subQ4=sQuery(id+"F0.wireOp",EDGE,"E2.right");var subQ5=sQuery(id+"F0.wireOp",EDGE,"E2.top");var subQ6=makeQuery(id+"F7.opExtrude","CAP_EDGE",EDGE,{"disambiguationData":[OSD([subQ5,subQ4,subQ1,subQ0,subQ3,subQ2])],"isStart":false});Q22=makeQuery(id+"F15.opExtrude","CAP_EDGE",EDGE,{"disambiguationData":[OSD([subQ5,subQ4,subQ1,subQ0,subQ3,subQ2]),TDD([makeQuery(id+"F14.imprint","IMPRINT",EDGE,{"derivedFrom":makeQuery(id+"F11.opExtrude","CAP_EDGE",EDGE,{"disambiguationData":[OSD([subQ5,subQ4,subQ1,subQ0,subQ3,subQ2]),TDD([makeQuery(id+"F10.imprint","IMPRINT",EDGE,{"disambiguationData":[TD([[makeQuery(id+"F10.imprint","INTERSECT",VERTEX,{"derivedFrom":[subQ6,sQuery(id+"F10.wireOp",EDGE,"E8")]}),-1.0]])],"derivedFrom":subQ6})])],"isStart":false})})])],"isStart":false});}
            var Q23;
            {var subQ0=sQuery(id+"F3.wireOp",EDGE,"E3.right");var subQ1=sQuery(id+"F3.wireOp",EDGE,"E3.bottom");var subQ2=sQuery(id+"F5.wireOp",EDGE,"E4.left");var subQ3=sQuery(id+"F5.wireOp",EDGE,"E4.bottom");var subQ4=sQuery(id+"F0.wireOp",EDGE,"E2.left");var subQ5=sQuery(id+"F0.wireOp",EDGE,"E2.top");var subQ6=makeQuery(id+"F7.opExtrude","CAP_EDGE",EDGE,{"disambiguationData":[OSD([subQ5,subQ4,subQ1,subQ0,subQ3,subQ2])],"isStart":false});Q23=makeQuery(id+"F15.opExtrude","CAP_EDGE",EDGE,{"disambiguationData":[OSD([subQ5,subQ4,subQ1,subQ0,subQ3,subQ2]),TDD([makeQuery(id+"F14.imprint","IMPRINT",EDGE,{"derivedFrom":makeQuery(id+"F9.opExtrude","CAP_EDGE",EDGE,{"disambiguationData":[OSD([subQ5,subQ4,subQ1,subQ0,subQ3,subQ2]),TDD([makeQuery(id+"F8.imprint","IMPRINT",EDGE,{"disambiguationData":[TD([[makeQuery(id+"F8.imprint","INTERSECT",VERTEX,{"derivedFrom":[subQ6,sQuery(id+"F8.wireOp",EDGE,"E5")]}),-1.0]])],"derivedFrom":subQ6})])],"isStart":false})})])],"isStart":false});}
            var Q24;
            {var subQ0=sQuery(id+"F5.wireOp",EDGE,"E4.left");var subQ1=sQuery(id+"F5.wireOp",EDGE,"E4.bottom");var subQ2=sQuery(id+"F3.wireOp",EDGE,"E3.right");var subQ3=sQuery(id+"F3.wireOp",EDGE,"E3.bottom");var subQ4=sQuery(id+"F0.wireOp",EDGE,"E2.left");var subQ5=sQuery(id+"F0.wireOp",EDGE,"E2.top");var subQ6=makeQuery(id+"F7.opExtrude","CAP_EDGE",EDGE,{"disambiguationData":[OSD([subQ5,subQ4,subQ3,subQ2,subQ1,subQ0])],"isStart":false});Q24=makeQuery(id+"F15.opExtrude","CAP_EDGE",EDGE,{"disambiguationData":[OSD([subQ5,subQ4,subQ3,subQ2,subQ1,subQ0]),TDD([makeQuery(id+"F14.imprint","IMPRINT",EDGE,{"derivedFrom":makeQuery(id+"F9.opExtrude","CAP_EDGE",EDGE,{"disambiguationData":[OSD([subQ5,subQ4,subQ3,subQ2,subQ1,subQ0]),TDD([makeQuery(id+"F8.imprint","IMPRINT",EDGE,{"disambiguationData":[TD([[makeQuery(id+"F8.imprint","INTERSECT",VERTEX,{"derivedFrom":[subQ6,sQuery(id+"F8.wireOp",EDGE,"E6")]}),1.0]])],"derivedFrom":subQ6})])],"isStart":false})})])],"isStart":false});}
            fillet(context, id + "F16", {"entities" : qUnion([Q0, Q1, Q2, Q3, Q4, Q5, Q6, Q7, Q8, Q9, Q10, Q11, Q12, Q13, Q14, Q15, Q16, Q17, Q18, Q19, Q20, Q21, Q22, Q23, Q24]), "radius" : 1 * mm, "tangentPropagation" : true, "allowEdgeOverflow" : false});
        }
        {
            var Q0;
            Q0=qCreatedBy(makeId("Front.planeOp"),FACE);
            var sketch = newSketch(context, id + "F17", { "sketchPlane" : qUnion([Q0])});
            skLineSegment(sketch, "E11", {"start": v(32.03, 0) * mm, "end": v(32.03, 69) * mm});
            skLineSegment(sketch, "E12", {"start": v(32.03, 69) * mm, "end": v(134.03, 69) * mm});
            skLineSegment(sketch, "E13", {"start": v(134.03, 69) * mm, "end": v(134.03, 0) * mm});
            skLineSegment(sketch, "E14", {"start": v(134.03, 0) * mm, "end": v(32.03, 0) * mm});
            skSolve(sketch);
        }
        {
            var Q0;
            Q0=makeQuery(id+"F17.imprint","IMPRINT",FACE,{"disambiguationData":[TD([[makeQuery(id+"F17.imprint","IMPRINT",EDGE,{"derivedFrom":sQuery(id+"F17.wireOp",EDGE,"E11")}),-1.0]])]});
            extrude(context, id + "F18", {"entities" : qUnion([Q0]), "depth" : 5 * mm, "offsetDistance" : 25 * mm});
        }
        {
            var Q0;
            Q0=makeQuery(id+"F18.opExtrude","CAP_FACE",FACE,{"disambiguationData":[OSD([sQuery(id+"F17.wireOp",EDGE,"E11"),sQuery(id+"F17.wireOp",EDGE,"E12"),sQuery(id+"F17.wireOp",EDGE,"E13"),sQuery(id+"F17.wireOp",EDGE,"E14")])],"isStart":true});
            var sketch = newSketch(context, id + "F19", { "sketchPlane" : qUnion([Q0])});
            skLineSegment(sketch, "E15", {"start": v(-134.03, 18) * mm, "end": v(-32.03, 18) * mm});
            skLineSegment(sketch, "E16", {"start": v(-34.03, 69) * mm, "end": v(-34.03, 18) * mm});
            skSolve(sketch);
        }
        {
            var Q0;
            {var subQ3=sQuery(id+"F19.wireOp",EDGE,"E16");Q0=makeQuery(id+"F19.imprint","IMPRINT",FACE,{"disambiguationData":[TD([[makeQuery(id+"F19.imprint","IMPRINT",EDGE,{"derivedFrom":subQ3}),-1.0]])]});}
            extrude(context, id + "F20", {"entities" : qUnion([Q0]), "operationType" : NewBodyOperationType.ADD, "depth" : 1.6 * mm, "offsetDistance" : 25 * mm});
        }
        {
            var Q0;
            Q0=makeQuery(id+"F18.opExtrude","CAP_FACE",FACE,{"disambiguationData":[OSD([sQuery(id+"F17.wireOp",EDGE,"E11"),sQuery(id+"F17.wireOp",EDGE,"E12"),sQuery(id+"F17.wireOp",EDGE,"E13"),sQuery(id+"F17.wireOp",EDGE,"E14")])],"isStart":false});
            var sketch = newSketch(context, id + "F21", { "sketchPlane" : qUnion([Q0])});
            skLineSegment(sketch, "E17", {"start": v(34.03, 69) * mm, "end": v(34.03, 0) * mm});
            skSolve(sketch);
        }
        {
            var Q0;
            {var subQ0=sQuery(id+"F21.wireOp",EDGE,"E17");Q0=makeQuery(id+"F21.imprint","IMPRINT",FACE,{"disambiguationData":[TD([[makeQuery(id+"F21.imprint","IMPRINT",EDGE,{"derivedFrom":subQ0}),1.0]])]});}
            extrude(context, id + "F22", {"entities" : qUnion([Q0]), "operationType" : NewBodyOperationType.ADD, "depth" : 1.6 * mm, "offsetDistance" : 25 * mm});
        }
        {
            var Q0;
            {var subQ0=sQuery(id+"F17.wireOp",EDGE,"E13");Q0=makeQuery(id+"F22.boolean.opBoolean","MERGE",FACE,{"derivedFrom":[makeQuery(id+"F20.boolean.opBoolean","MERGE",FACE,{"derivedFrom":[makeQuery(id+"F18.opExtrude","SWEPT_FACE",FACE,{"disambiguationData":[OSD([subQ0])]}),makeQuery(id+"F20.opExtrude","SWEPT_FACE",FACE,{"disambiguationData":[OSD([subQ0])]})]}),makeQuery(id+"F22.opExtrude","SWEPT_FACE",FACE,{"disambiguationData":[OSD([subQ0])]})]});}
            var sketch = newSketch(context, id + "F23", { "sketchPlane" : qUnion([Q0])});
            skLineSegment(sketch, "E18", {"start": v(0, 18) * mm, "end": v(0, 69) * mm});
            skPoint(sketch, "E18.endSnap0", {"position": v(-2.5, 69) * mm});
            skLineSegment(sketch, "E19", {"start": v(-5, 69) * mm, "end": v(-5, 0) * mm});
            skSolve(sketch);
        }
        {
            var Q0;
            {var subQ0=sQuery(id+"F23.wireOp",EDGE,"E18");Q0=makeQuery(id+"F23.imprint","IMPRINT",FACE,{"disambiguationData":[TD([[makeQuery(id+"F23.imprint","IMPRINT",EDGE,{"derivedFrom":subQ0}),-1.0]])]});}
            var Q1;
            {var subQ0=sQuery(id+"F23.wireOp",EDGE,"E19");Q1=makeQuery(id+"F23.imprint","IMPRINT",FACE,{"disambiguationData":[TD([[makeQuery(id+"F23.imprint","IMPRINT",EDGE,{"derivedFrom":subQ0}),-1.0]])]});}
            extrude(context, id + "F24", {"entities" : qUnion([Q0, Q1]), "operationType" : NewBodyOperationType.ADD, "depth" : 2 * mm, "offsetDistance" : 25 * mm});
        }
        {
            var Q0;
            Q0 = qSketchRegion(id + "F21", true);
            var Q1;
            {var subQ0=sQuery(id+"F17.wireOp",EDGE,"E13");var subQ1=sQuery(id+"F17.wireOp",EDGE,"E12");var subQ2=makeQuery(id+"F22.boolean.opBoolean","MERGE",EDGE,{"derivedFrom":[makeQuery(id+"F20.boolean.opBoolean","MERGE",EDGE,{"derivedFrom":[makeQuery(id+"F18.opExtrude","SWEPT_EDGE",EDGE,{"disambiguationData":[OSD([subQ1,subQ0])]}),makeQuery(id+"F20.opExtrude","SWEPT_EDGE",EDGE,{"disambiguationData":[OSD([subQ1,subQ0])]})]}),makeQuery(id+"F22.opExtrude","SWEPT_EDGE",EDGE,{"disambiguationData":[OSD([subQ1,subQ0])]})]});Q1=makeQuery(id+"F24.boolean.opBoolean","MERGE",FACE,{"derivedFrom":[makeQuery(id+"F22.boolean.opBoolean","MERGE",FACE,{"derivedFrom":[makeQuery(id+"F20.boolean.opBoolean","MERGE",FACE,{"derivedFrom":[makeQuery(id+"F18.opExtrude","SWEPT_FACE",FACE,{"disambiguationData":[OSD([subQ1])]}),makeQuery(id+"F20.opExtrude","SWEPT_FACE",FACE,{"disambiguationData":[OSD([subQ1])]})]}),makeQuery(id+"F22.opExtrude","SWEPT_FACE",FACE,{"disambiguationData":[OSD([subQ1])]})]}),makeQuery(id+"F24.opExtrude","SWEPT_FACE",FACE,{"disambiguationData":[OSD([subQ1,subQ0]),TDD([makeQuery(id+"F23.imprint","IMPRINT",EDGE,{"disambiguationData":[TD([[makeQuery(id+"F23.imprint","INTERSECT",VERTEX,{"derivedFrom":[makeQuery(id+"F20.opExtrude","CAP_EDGE",EDGE,{"disambiguationData":[OSD([subQ0])],"isStart":false}),subQ2]}),1.0]])],"derivedFrom":subQ2})])]}),makeQuery(id+"F24.opExtrude","SWEPT_FACE",FACE,{"disambiguationData":[OSD([subQ1,subQ0]),TDD([makeQuery(id+"F23.imprint","IMPRINT",EDGE,{"disambiguationData":[TD([[makeQuery(id+"F23.imprint","INTERSECT",VERTEX,{"derivedFrom":[makeQuery(id+"F22.opExtrude","CAP_EDGE",EDGE,{"disambiguationData":[OSD([subQ0])],"isStart":false}),subQ2]}),-1.0]])],"derivedFrom":subQ2})])]})]});}
            extrude(context, id + "F25", {"entities" : qUnion([Q0, Q1]), "operationType" : NewBodyOperationType.ADD, "depth" : 2 * mm, "offsetDistance" : 25 * mm});
        }
        {
            var Q0;
            Q0=makeQuery(id+"F25.opExtrude","CAP_FACE",FACE,{"disambiguationData":[OSD([sQuery(id+"F17.wireOp",EDGE,"E12"),sQuery(id+"F17.wireOp",EDGE,"E13")])],"isStart":false});
            var sketch = newSketch(context, id + "F26", { "sketchPlane" : qUnion([Q0])});
            skLineSegment(sketch, "E20", {"start": v(34.03, 0) * mm, "end": v(134.03, 0) * mm});
            skLineSegment(sketch, "E21", {"start": v(134.03, -5) * mm, "end": v(34.03, -5) * mm});
            skSolve(sketch);
        }
        {
            var Q0;
            Q0=makeQuery(id+"F26.imprint","IMPRINT",FACE,{"disambiguationData":[TD([[makeQuery(id+"F26.imprint","IMPRINT",EDGE,{"derivedFrom":sQuery(id+"F26.wireOp",EDGE,"E21")}),1.0]])]});
            var Q1;
            Q1=makeQuery(id+"F26.imprint","IMPRINT",FACE,{"disambiguationData":[TD([[makeQuery(id+"F26.imprint","IMPRINT",EDGE,{"derivedFrom":sQuery(id+"F26.wireOp",EDGE,"E20")}),1.0]])]});
            extrude(context, id + "F27", {"entities" : qUnion([Q0, Q1]), "operationType" : NewBodyOperationType.ADD, "depth" : 2 * mm, "offsetDistance" : 25 * mm});
        }
        {
            var Q0;
            {var subQ0=sQuery(id+"F17.wireOp",EDGE,"E13");var subQ1=sQuery(id+"F17.wireOp",EDGE,"E12");var subQ2=makeQuery(id+"F22.opExtrude","CAP_EDGE",EDGE,{"disambiguationData":[OSD([subQ0])],"isStart":false});Q0=makeQuery(id+"F27.boolean.opBoolean","MERGE",FACE,{"derivedFrom":[makeQuery(id+"F24.boolean.opBoolean","MERGE",FACE,{"derivedFrom":[makeQuery(id+"F22.opExtrude","CAP_FACE",FACE,{"disambiguationData":[OSD([subQ1,subQ0,sQuery(id+"F17.wireOp",EDGE,"E14"),sQuery(id+"F21.wireOp",EDGE,"E17")])],"isStart":false}),makeQuery(id+"F24.opExtrude","SWEPT_FACE",FACE,{"disambiguationData":[OSD([subQ0]),TDD([makeQuery(id+"F23.imprint","IMPRINT",EDGE,{"derivedFrom":subQ2})])]})]}),makeQuery(id+"F27.opExtrude","SWEPT_FACE",FACE,{"disambiguationData":[OSD([subQ1,subQ0]),TDD([makeQuery(id+"F26.imprint","IMPRINT",EDGE,{"derivedFrom":makeQuery(id+"F24.boolean.opBoolean","MERGE",EDGE,{"derivedFrom":[makeQuery(id+"F22.opExtrude","CAP_EDGE",EDGE,{"disambiguationData":[OSD([subQ1])],"isStart":false}),makeQuery(id+"F24.opExtrude","SWEPT_EDGE",EDGE,{"disambiguationData":[OSD([subQ1,subQ0]),TDD([makeQuery(id+"F23.imprint","INTERSECT",VERTEX,{"derivedFrom":[subQ2,makeQuery(id+"F22.boolean.opBoolean","MERGE",EDGE,{"derivedFrom":[makeQuery(id+"F20.boolean.opBoolean","MERGE",EDGE,{"derivedFrom":[makeQuery(id+"F18.opExtrude","SWEPT_EDGE",EDGE,{"disambiguationData":[OSD([subQ1,subQ0])]}),makeQuery(id+"F20.opExtrude","SWEPT_EDGE",EDGE,{"disambiguationData":[OSD([subQ1,subQ0])]})]}),makeQuery(id+"F22.opExtrude","SWEPT_EDGE",EDGE,{"disambiguationData":[OSD([subQ1,subQ0])]})]})]})])]})]})})])]})]});}
            var Q1;
            {var subQ0=sQuery(id+"F17.wireOp",EDGE,"E13");var subQ1=sQuery(id+"F17.wireOp",EDGE,"E12");var subQ2=makeQuery(id+"F22.boolean.opBoolean","MERGE",EDGE,{"derivedFrom":[makeQuery(id+"F20.boolean.opBoolean","MERGE",EDGE,{"derivedFrom":[makeQuery(id+"F18.opExtrude","SWEPT_EDGE",EDGE,{"disambiguationData":[OSD([subQ1,subQ0])]}),makeQuery(id+"F20.opExtrude","SWEPT_EDGE",EDGE,{"disambiguationData":[OSD([subQ1,subQ0])]})]}),makeQuery(id+"F22.opExtrude","SWEPT_EDGE",EDGE,{"disambiguationData":[OSD([subQ1,subQ0])]})]});Q1=makeQuery(id+"F27.opExtrude","CAP_EDGE",EDGE,{"disambiguationData":[OSD([subQ1,subQ0]),TDD([makeQuery(id+"F26.imprint","IMPRINT",EDGE,{"derivedFrom":makeQuery(id+"F24.opExtrude","CAP_EDGE",EDGE,{"disambiguationData":[OSD([subQ1,subQ0]),TDD([makeQuery(id+"F23.imprint","IMPRINT",EDGE,{"disambiguationData":[TD([[makeQuery(id+"F23.imprint","INTERSECT",VERTEX,{"derivedFrom":[makeQuery(id+"F22.opExtrude","CAP_EDGE",EDGE,{"disambiguationData":[OSD([subQ0])],"isStart":false}),subQ2]}),-1.0]])],"derivedFrom":subQ2})])],"isStart":false})})])],"isStart":false});}
            var Q2;
            {var subQ0=sQuery(id+"F17.wireOp",EDGE,"E13");var subQ1=sQuery(id+"F17.wireOp",EDGE,"E12");var subQ2=makeQuery(id+"F22.boolean.opBoolean","MERGE",EDGE,{"derivedFrom":[makeQuery(id+"F20.boolean.opBoolean","MERGE",EDGE,{"derivedFrom":[makeQuery(id+"F18.opExtrude","SWEPT_EDGE",EDGE,{"disambiguationData":[OSD([subQ1,subQ0])]}),makeQuery(id+"F20.opExtrude","SWEPT_EDGE",EDGE,{"disambiguationData":[OSD([subQ1,subQ0])]})]}),makeQuery(id+"F22.opExtrude","SWEPT_EDGE",EDGE,{"disambiguationData":[OSD([subQ1,subQ0])]})]});Q2=makeQuery(id+"F27.opExtrude","CAP_EDGE",EDGE,{"disambiguationData":[OSD([subQ1,subQ0]),TDD([makeQuery(id+"F26.imprint","IMPRINT",EDGE,{"derivedFrom":makeQuery(id+"F24.opExtrude","CAP_EDGE",EDGE,{"disambiguationData":[OSD([subQ1,subQ0]),TDD([makeQuery(id+"F23.imprint","IMPRINT",EDGE,{"disambiguationData":[TD([[makeQuery(id+"F23.imprint","INTERSECT",VERTEX,{"derivedFrom":[makeQuery(id+"F20.opExtrude","CAP_EDGE",EDGE,{"disambiguationData":[OSD([subQ0])],"isStart":false}),subQ2]}),1.0]])],"derivedFrom":subQ2})])],"isStart":false})})])],"isStart":false});}
            var Q3;
            Q3=makeQuery(id+"F27.opExtrude","CAP_EDGE",EDGE,{"disambiguationData":[OSD([sQuery(id+"F17.wireOp",EDGE,"E12"),sQuery(id+"F21.wireOp",EDGE,"E17")])],"isStart":false});
            var Q4;
            Q4=makeQuery(id+"F22.opExtrude","SWEPT_EDGE",EDGE,{"disambiguationData":[OSD([sQuery(id+"F17.wireOp",EDGE,"E14"),sQuery(id+"F21.wireOp",EDGE,"E17")])]});
            var Q5;
            Q5=makeQuery(id+"F24.opExtrude","CAP_EDGE",EDGE,{"disambiguationData":[OSD([sQuery(id+"F17.wireOp",EDGE,"E13"),sQuery(id+"F17.wireOp",EDGE,"E14")])],"isStart":false});
            var Q6;
            {var subQ0=sQuery(id+"F17.wireOp",EDGE,"E13");var subQ1=sQuery(id+"F17.wireOp",EDGE,"E12");var subQ2=makeQuery(id+"F20.opExtrude","CAP_EDGE",EDGE,{"disambiguationData":[OSD([subQ0])],"isStart":false});Q6=makeQuery(id+"F27.boolean.opBoolean","MERGE",FACE,{"derivedFrom":[makeQuery(id+"F24.boolean.opBoolean","MERGE",FACE,{"derivedFrom":[makeQuery(id+"F20.opExtrude","CAP_FACE",FACE,{"disambiguationData":[OSD([subQ1,subQ0,sQuery(id+"F19.wireOp",EDGE,"E15"),sQuery(id+"F19.wireOp",EDGE,"E16")])],"isStart":false}),makeQuery(id+"F24.opExtrude","SWEPT_FACE",FACE,{"disambiguationData":[OSD([subQ0]),TDD([makeQuery(id+"F23.imprint","IMPRINT",EDGE,{"derivedFrom":subQ2})])]})]}),makeQuery(id+"F27.opExtrude","SWEPT_FACE",FACE,{"disambiguationData":[OSD([subQ1,subQ0]),TDD([makeQuery(id+"F26.imprint","IMPRINT",EDGE,{"derivedFrom":makeQuery(id+"F24.boolean.opBoolean","MERGE",EDGE,{"derivedFrom":[makeQuery(id+"F20.opExtrude","CAP_EDGE",EDGE,{"disambiguationData":[OSD([subQ1])],"isStart":false}),makeQuery(id+"F24.opExtrude","SWEPT_EDGE",EDGE,{"disambiguationData":[OSD([subQ1,subQ0]),TDD([makeQuery(id+"F23.imprint","INTERSECT",VERTEX,{"derivedFrom":[subQ2,makeQuery(id+"F22.boolean.opBoolean","MERGE",EDGE,{"derivedFrom":[makeQuery(id+"F20.boolean.opBoolean","MERGE",EDGE,{"derivedFrom":[makeQuery(id+"F18.opExtrude","SWEPT_EDGE",EDGE,{"disambiguationData":[OSD([subQ1,subQ0])]}),makeQuery(id+"F20.opExtrude","SWEPT_EDGE",EDGE,{"disambiguationData":[OSD([subQ1,subQ0])]})]}),makeQuery(id+"F22.opExtrude","SWEPT_EDGE",EDGE,{"disambiguationData":[OSD([subQ1,subQ0])]})]})]})])]})]})})])]})]});}
            var Q7;
            Q7=makeQuery(id+"F20.opExtrude","SWEPT_EDGE",EDGE,{"disambiguationData":[OSD([sQuery(id+"F19.wireOp",EDGE,"E15"),sQuery(id+"F19.wireOp",EDGE,"E16")])]});
            var Q8;
            Q8=makeQuery(id+"F27.opExtrude","CAP_EDGE",EDGE,{"disambiguationData":[OSD([sQuery(id+"F17.wireOp",EDGE,"E12"),sQuery(id+"F19.wireOp",EDGE,"E16")])],"isStart":false});
            var Q9;
            Q9=makeQuery(id+"F24.opExtrude","CAP_EDGE",EDGE,{"disambiguationData":[OSD([sQuery(id+"F17.wireOp",EDGE,"E13"),sQuery(id+"F19.wireOp",EDGE,"E15")])],"isStart":false});
            var Q10;
            {var subQ0=sQuery(id+"F17.wireOp",EDGE,"E13");var subQ1=sQuery(id+"F17.wireOp",EDGE,"E12");var subQ2=makeQuery(id+"F22.boolean.opBoolean","MERGE",EDGE,{"derivedFrom":[makeQuery(id+"F20.boolean.opBoolean","MERGE",EDGE,{"derivedFrom":[makeQuery(id+"F18.opExtrude","SWEPT_EDGE",EDGE,{"disambiguationData":[OSD([subQ1,subQ0])]}),makeQuery(id+"F20.opExtrude","SWEPT_EDGE",EDGE,{"disambiguationData":[OSD([subQ1,subQ0])]})]}),makeQuery(id+"F22.opExtrude","SWEPT_EDGE",EDGE,{"disambiguationData":[OSD([subQ1,subQ0])]})]});Q10=makeQuery(id+"F27.opExtrude","CAP_EDGE",EDGE,{"disambiguationData":[OSD([subQ1,subQ0]),TDD([makeQuery(id+"F26.imprint","IMPRINT",EDGE,{"derivedFrom":makeQuery(id+"F25.opExtrude","CAP_EDGE",EDGE,{"disambiguationData":[OSD([subQ1,subQ0]),TDD([makeQuery(id+"F24.opExtrude","CAP_EDGE",EDGE,{"disambiguationData":[OSD([subQ1,subQ0]),TDD([makeQuery(id+"F23.imprint","IMPRINT",EDGE,{"disambiguationData":[TD([[makeQuery(id+"F23.imprint","INTERSECT",VERTEX,{"derivedFrom":[makeQuery(id+"F20.opExtrude","CAP_EDGE",EDGE,{"disambiguationData":[OSD([subQ0])],"isStart":false}),subQ2]}),1.0]])],"derivedFrom":subQ2})])],"isStart":false})])],"isStart":false})})])],"isStart":false});}
            var Q11;
            {var subQ0=sQuery(id+"F17.wireOp",EDGE,"E13");var subQ1=sQuery(id+"F17.wireOp",EDGE,"E12");var subQ2=makeQuery(id+"F22.boolean.opBoolean","MERGE",EDGE,{"derivedFrom":[makeQuery(id+"F20.boolean.opBoolean","MERGE",EDGE,{"derivedFrom":[makeQuery(id+"F18.opExtrude","SWEPT_EDGE",EDGE,{"disambiguationData":[OSD([subQ1,subQ0])]}),makeQuery(id+"F20.opExtrude","SWEPT_EDGE",EDGE,{"disambiguationData":[OSD([subQ1,subQ0])]})]}),makeQuery(id+"F22.opExtrude","SWEPT_EDGE",EDGE,{"disambiguationData":[OSD([subQ1,subQ0])]})]});Q11=makeQuery(id+"F27.opExtrude","CAP_EDGE",EDGE,{"disambiguationData":[OSD([subQ1,subQ0]),TDD([makeQuery(id+"F26.imprint","IMPRINT",EDGE,{"derivedFrom":makeQuery(id+"F25.opExtrude","CAP_EDGE",EDGE,{"disambiguationData":[OSD([subQ1,subQ0]),TDD([makeQuery(id+"F24.opExtrude","CAP_EDGE",EDGE,{"disambiguationData":[OSD([subQ1,subQ0]),TDD([makeQuery(id+"F23.imprint","IMPRINT",EDGE,{"disambiguationData":[TD([[makeQuery(id+"F23.imprint","INTERSECT",VERTEX,{"derivedFrom":[makeQuery(id+"F22.opExtrude","CAP_EDGE",EDGE,{"disambiguationData":[OSD([subQ0])],"isStart":false}),subQ2]}),-1.0]])],"derivedFrom":subQ2})])],"isStart":false})])],"isStart":false})})])],"isStart":false});}
            var Q12;
            {var subQ0=sQuery(id+"F17.wireOp",EDGE,"E13");var subQ1=sQuery(id+"F17.wireOp",EDGE,"E12");Q12=makeQuery(id+"F25.opExtrude","CAP_EDGE",EDGE,{"disambiguationData":[OSD([subQ1,subQ0]),TDD([makeQuery(id+"F22.boolean.opBoolean","MERGE",EDGE,{"derivedFrom":[makeQuery(id+"F20.boolean.opBoolean","MERGE",EDGE,{"derivedFrom":[makeQuery(id+"F18.opExtrude","SWEPT_EDGE",EDGE,{"disambiguationData":[OSD([subQ1,subQ0])]}),makeQuery(id+"F20.opExtrude","SWEPT_EDGE",EDGE,{"disambiguationData":[OSD([subQ1,subQ0])]})]}),makeQuery(id+"F22.opExtrude","SWEPT_EDGE",EDGE,{"disambiguationData":[OSD([subQ1,subQ0])]})]})])],"isStart":false});}
            fillet(context, id + "F28", {"entities" : qUnion([Q0, Q1, Q2, Q3, Q4, Q5, Q6, Q7, Q8, Q9, Q10, Q11, Q12]), "radius" : 1 * mm, "tangentPropagation" : true, "allowEdgeOverflow" : false});
        }
        {
            var Q0;
            Q0=makeQuery(id+"F18.opExtrude","SWEPT_BODY",BODY,{"disambiguationData":[OSD([sQuery(id+"F17.wireOp",EDGE,"E11"),sQuery(id+"F17.wireOp",EDGE,"E12"),sQuery(id+"F17.wireOp",EDGE,"E13"),sQuery(id+"F17.wireOp",EDGE,"E14")])]});
            var Q1;
            Q1=qCreatedBy(makeId("Right.planeOp"),FACE);
            mirror(context, id + "F29", {"entities" : qUnion([Q0]), "mirrorPlane" : qUnion([Q1])});
        }
    });
